# Revit family: Faucet-Wall_Mount-Lavatory-KALLISTA-Guise-P34236
name_source: partatom
category: Plumbing Fixtures
units: mm (PartAtom-declared; Revit-internal decimal feet)

## family parameters
Cut with Voids When Loaded = No
Host = Face
OmniClass Number = 23.31.11.00
OmniClass Title = Faucets
Part Type = Normal
Room Calculation Point = No
Round Connector Dimension = Use Diameter
Shared = No

## types (6) — shared parameters
ADA Compliant = No
Assembly Code = D2010
CW Connection = Yes
Cold Water Inlet = Cold Water Inlet
Date Modified = 06/29/2024
Default Elevation = 36"
Description = Wall Mount Sink Faucet, Wide Spread
Drain Included = Yes
Flow Rate = 1 GPM
HW Connection = Yes
Handle Clearance = 1 15/16"
Height = 2 1/8"
Hot Water Inlet = Hot Water Inlet
Length = 8 3/16"
Manufacturer = Kallista Co.
Master Format 2014 = 22 41 39
Master Format 2014 Name = Residential Faucets, Supplies, and Trim
Material = Premium Metal Construction
Pressure = 0.00 psi
Product Name = Guise
Spout Reach = 8 3/16"
URL = https://www.kallista.com
Vent Connection = No
Waste Connection = No
Waste Water Outlet = Waste Water Outlet
WaterSense Certified = No

## per-type parameters (varying)
| type | Finish | Model | Type |
| BAF-Brushed French Gold | Kallista-Metal-BAF-Brushed_French_Gold | P34236-LV-BAF | 1 |
| BN-Brushed Nickel | Kallista-Metal-BN-Brushed_Nickel | P34236-LV-BN | 2 |
| CP-Chrome | Kallista-Metal-CP-Chrome | P34236-LV-CP | 3 |
| SN-Polished Nickel | Kallista-Metal-SN-Polished_Nickel | P34236-LV-SN | 6 |
| GHP | <By Category> | P34236-LV-GHP | 4 |
| PGP-Polished Graphite | Kallista-Metal-PGP-Polished_Graphite | P34236-LV-PGP | 5 |

## geometry (parser evidence)
native form markers: Sweep x8
no freeform markers — native parametric forms only
